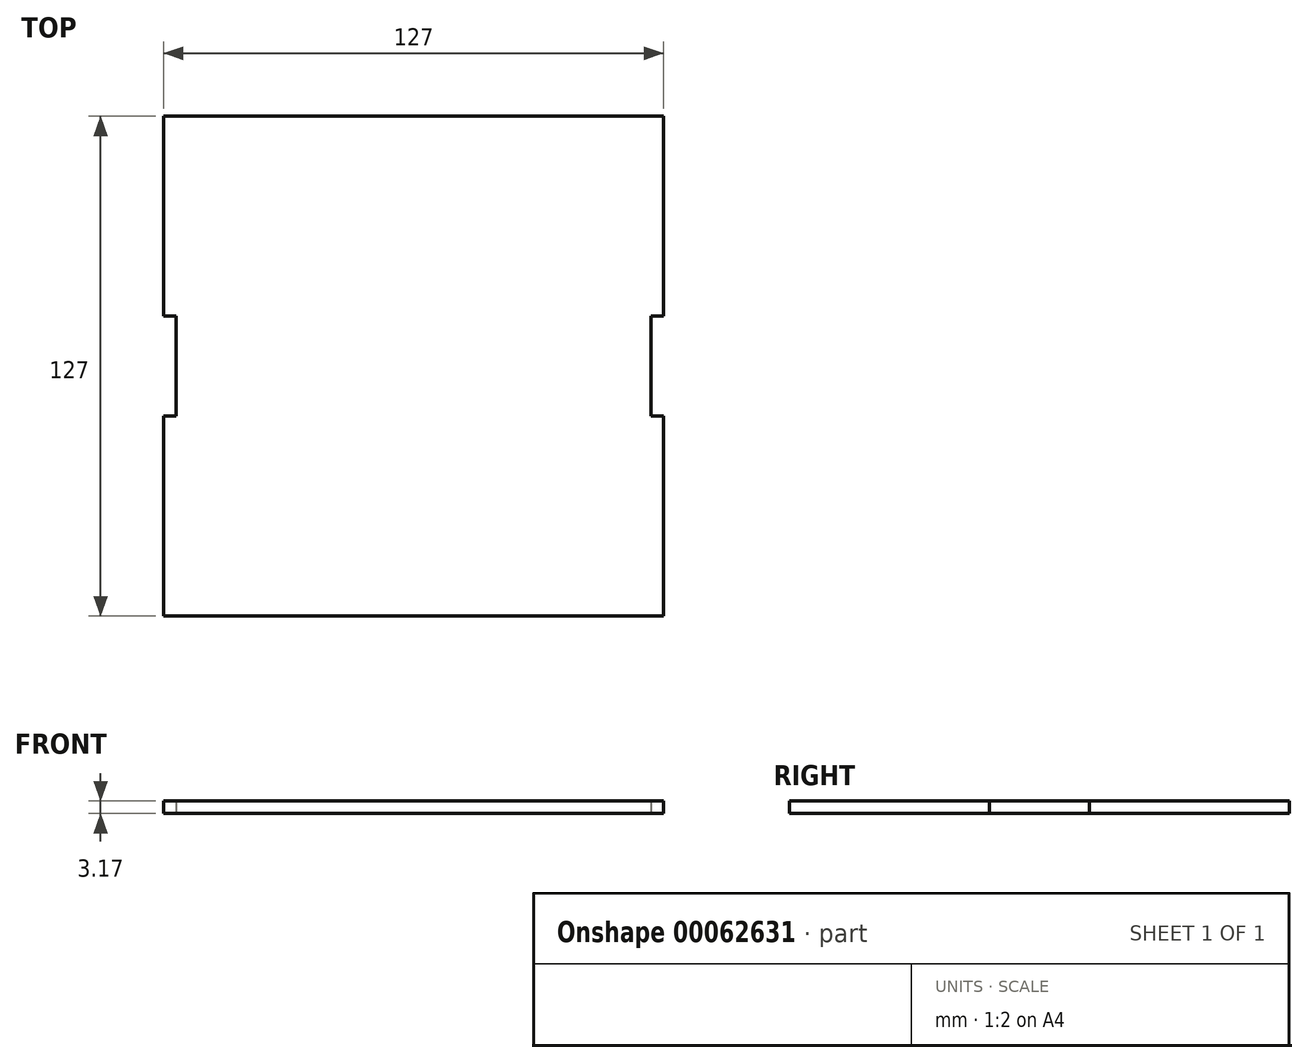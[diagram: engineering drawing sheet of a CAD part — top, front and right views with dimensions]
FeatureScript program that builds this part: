
annotation { "Feature Type Name" : "Feature", "Feature Type Description" : "" }
export const myFeature = defineFeature(function(context is Context, id is Id, definition is map)
    precondition{}
    {
        {
            var Q0;
            Q0=qCreatedBy(makeId("Top.planeOp"),FACE);
            var sketch = newSketch(context, id + "F0", { "sketchPlane" : qUnion([Q0])});
            skLineSegment(sketch, "E0.bottom", {"start": v(-57.89, 57.9) * mm, "end": v(69.11, 57.9) * mm});
            skLineSegment(sketch, "E0.top", {"start": v(-57.89, -69.1) * mm, "end": v(69.11, -69.1) * mm});
            skLineSegment(sketch, "E1.bottom", {"start": v(-57.89, -18.3) * mm, "end": v(-54.71, -18.3) * mm});
            skLineSegment(sketch, "E1.top", {"start": v(-57.89, 7.1) * mm, "end": v(-54.71, 7.1) * mm});
            skLineSegment(sketch, "E1.right", {"start": v(-54.71, -18.3) * mm, "end": v(-54.71, 7.1) * mm});
            skLineSegment(sketch, "E2", {"start": v(-57.89, -69.1) * mm, "end": v(-57.89, -18.3) * mm});
            skLineSegment(sketch, "E3", {"start": v(-57.89, 7.1) * mm, "end": v(-57.89, 57.9) * mm});
            skLineSegment(sketch, "E4.bottom", {"start": v(69.11, -18.3) * mm, "end": v(65.94, -18.3) * mm});
            skLineSegment(sketch, "E4.top", {"start": v(69.11, 7.1) * mm, "end": v(65.94, 7.1) * mm});
            skLineSegment(sketch, "E4.right", {"start": v(65.94, -18.3) * mm, "end": v(65.94, 7.1) * mm});
            skLineSegment(sketch, "E5", {"start": v(69.11, -69.1) * mm, "end": v(69.11, -18.3) * mm});
            skLineSegment(sketch, "E6", {"start": v(69.11, 7.1) * mm, "end": v(69.11, 57.9) * mm});
            skSolve(sketch);
        }
        {
            var Q0;
            Q0=makeQuery(id+"F0.imprint","IMPRINT",FACE,{"disambiguationData":[TD([[makeQuery(id+"F0.imprint","IMPRINT",EDGE,{"derivedFrom":sQuery(id+"F0.wireOp",EDGE,"E0.bottom")}),-1.0]])]});
            extrude(context, id + "F1", {"entities" : qUnion([Q0]), "depth" : 3.17 * mm});
        }
    });
